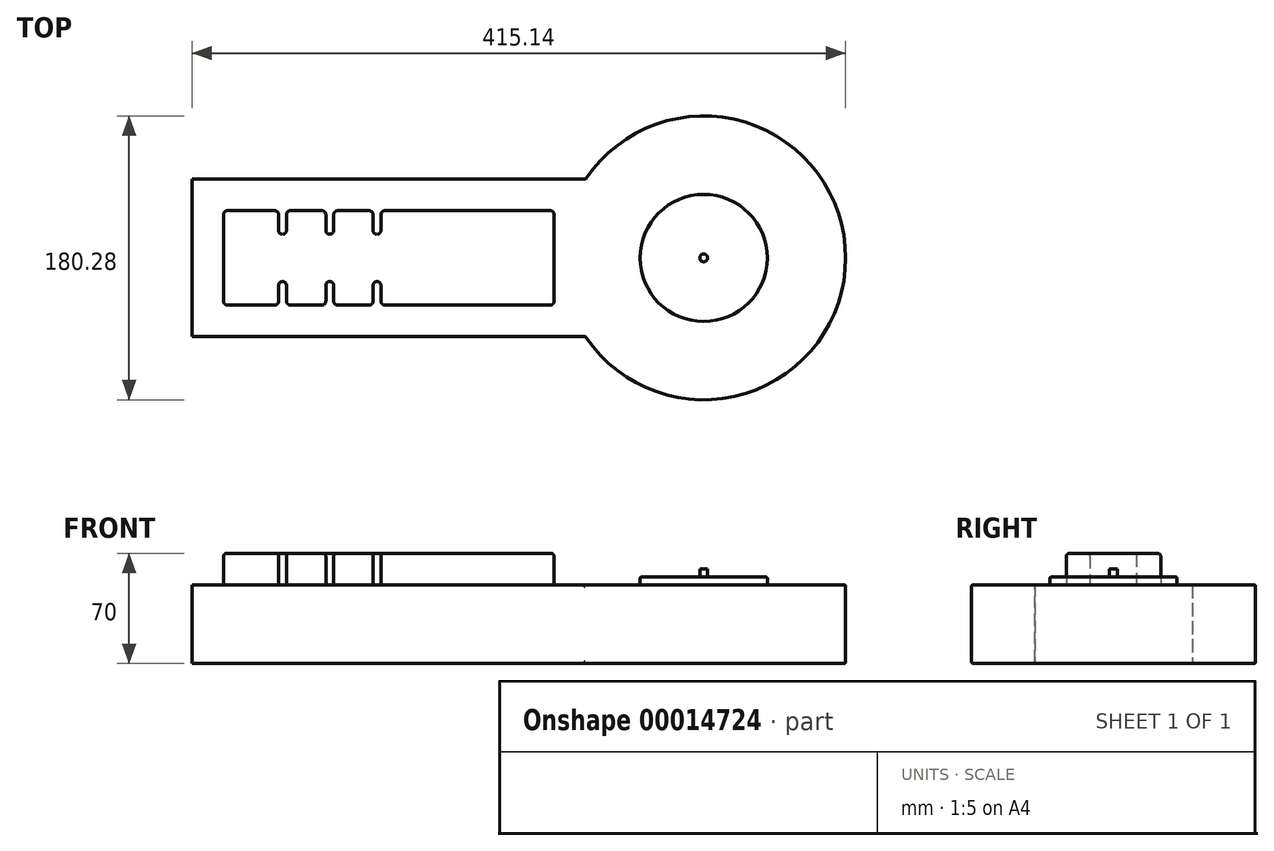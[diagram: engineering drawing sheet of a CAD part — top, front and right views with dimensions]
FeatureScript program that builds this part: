
annotation { "Feature Type Name" : "Feature", "Feature Type Description" : "" }
export const myFeature = defineFeature(function(context is Context, id is Id, definition is map)
    precondition{}
    {
        {
            var Q0;
            Q0=qCreatedBy(makeId("Top.planeOp"),FACE);
            var sketch = newSketch(context, id + "F0", { "sketchPlane" : qUnion([Q0])});
            skLineSegment(sketch, "E0.bottom", {"start": v(0, 0) * mm, "end": v(250, 0) * mm});
            skLineSegment(sketch, "E0.top", {"start": v(0, 100) * mm, "end": v(250, 100) * mm});
            skLineSegment(sketch, "E0.left", {"start": v(0, 0) * mm, "end": v(0, 100) * mm});
            skLineSegment(sketch, "E0.right", {"start": v(250, 0) * mm, "end": v(250, 100) * mm});
            skArc(sketch, "E1", {"start": v(250, 0) * mm, "mid": v(415.14, 50) * mm, "end": v(250, 100) * mm});
            skSolve(sketch);
        }
        {
            var Q0;
            Q0=makeQuery(id+"F0.imprint","IMPRINT",FACE,{"disambiguationData":[TD([[makeQuery(id+"F0.imprint","IMPRINT",EDGE,{"derivedFrom":sQuery(id+"F0.wireOp",EDGE,"E0.bottom")}),1.0]])]});
            var Q1;
            Q1=makeQuery(id+"F0.imprint","IMPRINT",FACE,{"disambiguationData":[TD([[makeQuery(id+"F0.imprint","IMPRINT",EDGE,{"derivedFrom":sQuery(id+"F0.wireOp",EDGE,"E0.right")}),-1.0]])]});
            extrude(context, id + "F1", {"entities" : qUnion([Q0, Q1]), "depth" : 50 * mm});
        }
        {
            var Q0;
            Q0=makeQuery(id+"F1.opExtrude","CAP_FACE",FACE,{"disambiguationData":[OSD([sQuery(id+"F0.wireOp",EDGE,"E0.bottom"),sQuery(id+"F0.wireOp",EDGE,"E0.top"),sQuery(id+"F0.wireOp",EDGE,"E0.left"),sQuery(id+"F0.wireOp",EDGE,"E1")])],"isStart":false});
            var sketch = newSketch(context, id + "F2", { "sketchPlane" : qUnion([Q0])});
            skLineSegment(sketch, "E2.bottom", {"start": v(20, 80) * mm, "end": v(230, 80) * mm});
            skLineSegment(sketch, "E2.top", {"start": v(20, 20) * mm, "end": v(230, 20) * mm});
            skLineSegment(sketch, "E2.left", {"start": v(20, 80) * mm, "end": v(20, 20) * mm});
            skLineSegment(sketch, "E2.right", {"start": v(230, 80) * mm, "end": v(230, 20) * mm});
            skLineSegment(sketch, "E3.bottom", {"start": v(55, 80) * mm, "end": v(60, 80) * mm});
            skLineSegment(sketch, "E3.top", {"start": v(55, 65) * mm, "end": v(60, 65) * mm});
            skLineSegment(sketch, "E3.left", {"start": v(55, 80) * mm, "end": v(55, 65) * mm});
            skLineSegment(sketch, "E3.right", {"start": v(60, 80) * mm, "end": v(60, 65) * mm});
            skLineSegment(sketch, "E4.bottom", {"start": v(85, 80) * mm, "end": v(90, 80) * mm});
            skLineSegment(sketch, "E4.top", {"start": v(85, 65) * mm, "end": v(90, 65) * mm});
            skLineSegment(sketch, "E4.left", {"start": v(85, 80) * mm, "end": v(85, 65) * mm});
            skLineSegment(sketch, "E4.right", {"start": v(90, 80) * mm, "end": v(90, 65) * mm});
            skLineSegment(sketch, "E5.bottom", {"start": v(115, 80) * mm, "end": v(120, 80) * mm});
            skLineSegment(sketch, "E5.top", {"start": v(115, 65) * mm, "end": v(120, 65) * mm});
            skLineSegment(sketch, "E5.left", {"start": v(115, 80) * mm, "end": v(115, 65) * mm});
            skLineSegment(sketch, "E5.right", {"start": v(120, 80) * mm, "end": v(120, 65) * mm});
            skLineSegment(sketch, "E6.bottom", {"start": v(55, 20) * mm, "end": v(60, 20) * mm});
            skLineSegment(sketch, "E6.top", {"start": v(55, 35) * mm, "end": v(60, 35) * mm});
            skLineSegment(sketch, "E6.left", {"start": v(55, 20) * mm, "end": v(55, 35) * mm});
            skLineSegment(sketch, "E6.right", {"start": v(60, 20) * mm, "end": v(60, 35) * mm});
            skLineSegment(sketch, "E7.bottom", {"start": v(85, 20) * mm, "end": v(90, 20) * mm});
            skLineSegment(sketch, "E7.top", {"start": v(85, 35) * mm, "end": v(90, 35) * mm});
            skLineSegment(sketch, "E7.left", {"start": v(85, 20) * mm, "end": v(85, 35) * mm});
            skLineSegment(sketch, "E7.right", {"start": v(90, 20) * mm, "end": v(90, 35) * mm});
            skLineSegment(sketch, "E8.bottom", {"start": v(115, 20) * mm, "end": v(120, 20) * mm});
            skLineSegment(sketch, "E8.top", {"start": v(115, 35) * mm, "end": v(120, 35) * mm});
            skLineSegment(sketch, "E8.left", {"start": v(115, 20) * mm, "end": v(115, 35) * mm});
            skLineSegment(sketch, "E8.right", {"start": v(120, 20) * mm, "end": v(120, 35) * mm});
            skSolve(sketch);
        }
        {
            var Q0;
            {var subQ20=sQuery(id+"F2.wireOp",EDGE,"E2.left");Q0=makeQuery(id+"F2.imprint","IMPRINT",FACE,{"disambiguationData":[TD([[makeQuery(id+"F2.imprint","IMPRINT",EDGE,{"derivedFrom":subQ20}),1.0]])]});}
            extrude(context, id + "F3", {"entities" : qUnion([Q0]), "operationType" : NewBodyOperationType.ADD, "depth" : 20 * mm});
        }
        {
            var Q0;
            Q0=makeQuery(id+"F1.opExtrude","CAP_FACE",FACE,{"disambiguationData":[OSD([sQuery(id+"F0.wireOp",EDGE,"E0.bottom"),sQuery(id+"F0.wireOp",EDGE,"E0.top"),sQuery(id+"F0.wireOp",EDGE,"E0.left"),sQuery(id+"F0.wireOp",EDGE,"E1")])],"isStart":false});
            var sketch = newSketch(context, id + "F4", { "sketchPlane" : qUnion([Q0])});
            skCircle(sketch, "E9", {"center": v(325, 50) * mm, "radius": 40.38 * mm});
            skSolve(sketch);
        }
        {
            var Q0;
            Q0=qSketchRegion(id+"F4",true);
            extrude(context, id + "F5", {"entities" : qUnion([Q0]), "operationType" : NewBodyOperationType.ADD, "depth" : 5 * mm});
        }
        {
            var Q0;
            Q0=makeQuery(id+"F5.opExtrude","CAP_FACE",FACE,{"disambiguationData":[OSD([sQuery(id+"F4.wireOp",EDGE,"E9")])],"isStart":false});
            var sketch = newSketch(context, id + "F6", { "sketchPlane" : qUnion([Q0])});
            skCircle(sketch, "E10", {"center": v(325, 50) * mm, "radius": 2.5 * mm});
            skSolve(sketch);
        }
        {
            var Q0;
            Q0=makeQuery(id+"F6.imprint","IMPRINT",FACE,{"disambiguationData":[TD([[makeQuery(id+"F6.imprint","IMPRINT",EDGE,{"derivedFrom":sQuery(id+"F6.wireOp",EDGE,"E10")}),1.0]])]});
            extrude(context, id + "F7", {"entities" : qUnion([Q0]), "operationType" : NewBodyOperationType.ADD, "depth" : 5 * mm});
        }
        {
            var Q0;
            Q0=makeQuery(id+"F1.opExtrude","SWEPT_FACE",FACE,{"disambiguationData":[OSD([sQuery(id+"F0.wireOp",EDGE,"E1")])]});
            var Q1;
            Q1=makeQuery(id+"F5.opExtrude","CAP_EDGE",EDGE,{"disambiguationData":[OSD([sQuery(id+"F4.wireOp",EDGE,"E9")])],"isStart":false});
            var Q2;
            Q2=makeQuery(id+"F5.opExtrude","CAP_EDGE",EDGE,{"disambiguationData":[OSD([sQuery(id+"F4.wireOp",EDGE,"E9")])],"isStart":true});
            fillet(context, id + "F8", {"entities" : qUnion([Q0, Q1, Q2]), "radius" : 1 * mm, "tangentPropagation" : true, "allowEdgeOverflow" : false});
        }
        {
            var Q0;
            Q0=makeQuery(id+"F3.opExtrude","SWEPT_EDGE",EDGE,{"disambiguationData":[OSD([sQuery(id+"F2.wireOp",EDGE,"E6.top"),sQuery(id+"F2.wireOp",EDGE,"E6.left")])]});
            var Q1;
            Q1=makeQuery(id+"F3.opExtrude","SWEPT_EDGE",EDGE,{"disambiguationData":[OSD([sQuery(id+"F2.wireOp",EDGE,"E2.top"),sQuery(id+"F2.wireOp",EDGE,"E6.bottom"),sQuery(id+"F2.wireOp",EDGE,"E6.left")])]});
            var Q2;
            Q2=makeQuery(id+"F3.opExtrude","SWEPT_EDGE",EDGE,{"disambiguationData":[OSD([sQuery(id+"F2.wireOp",EDGE,"E6.top"),sQuery(id+"F2.wireOp",EDGE,"E6.right")])]});
            var Q3;
            Q3=makeQuery(id+"F3.opExtrude","SWEPT_EDGE",EDGE,{"disambiguationData":[OSD([sQuery(id+"F2.wireOp",EDGE,"E2.top"),sQuery(id+"F2.wireOp",EDGE,"E6.bottom"),sQuery(id+"F2.wireOp",EDGE,"E6.right")])]});
            var Q4;
            Q4=makeQuery(id+"F3.opExtrude","SWEPT_EDGE",EDGE,{"disambiguationData":[OSD([sQuery(id+"F2.wireOp",EDGE,"E2.top"),sQuery(id+"F2.wireOp",EDGE,"E7.bottom"),sQuery(id+"F2.wireOp",EDGE,"E7.left")])]});
            var Q5;
            Q5=makeQuery(id+"F3.opExtrude","SWEPT_EDGE",EDGE,{"disambiguationData":[OSD([sQuery(id+"F2.wireOp",EDGE,"E7.top"),sQuery(id+"F2.wireOp",EDGE,"E7.right")])]});
            var Q6;
            Q6=makeQuery(id+"F3.opExtrude","SWEPT_EDGE",EDGE,{"disambiguationData":[OSD([sQuery(id+"F2.wireOp",EDGE,"E2.top"),sQuery(id+"F2.wireOp",EDGE,"E7.bottom"),sQuery(id+"F2.wireOp",EDGE,"E7.right")])]});
            var Q7;
            Q7=makeQuery(id+"F3.opExtrude","SWEPT_EDGE",EDGE,{"disambiguationData":[OSD([sQuery(id+"F2.wireOp",EDGE,"E2.top"),sQuery(id+"F2.wireOp",EDGE,"E8.bottom"),sQuery(id+"F2.wireOp",EDGE,"E8.left")])]});
            var Q8;
            Q8=makeQuery(id+"F3.opExtrude","SWEPT_EDGE",EDGE,{"disambiguationData":[OSD([sQuery(id+"F2.wireOp",EDGE,"E8.top"),sQuery(id+"F2.wireOp",EDGE,"E8.right")])]});
            var Q9;
            Q9=makeQuery(id+"F3.opExtrude","SWEPT_EDGE",EDGE,{"disambiguationData":[OSD([sQuery(id+"F2.wireOp",EDGE,"E2.top"),sQuery(id+"F2.wireOp",EDGE,"E8.bottom"),sQuery(id+"F2.wireOp",EDGE,"E8.right")])]});
            var Q10;
            Q10=makeQuery(id+"F3.opExtrude","SWEPT_EDGE",EDGE,{"disambiguationData":[OSD([sQuery(id+"F2.wireOp",EDGE,"E7.top"),sQuery(id+"F2.wireOp",EDGE,"E7.left")])]});
            var Q11;
            Q11=makeQuery(id+"F3.opExtrude","SWEPT_EDGE",EDGE,{"disambiguationData":[OSD([sQuery(id+"F2.wireOp",EDGE,"E8.top"),sQuery(id+"F2.wireOp",EDGE,"E8.left")])]});
            var Q12;
            Q12=makeQuery(id+"F3.opExtrude","SWEPT_EDGE",EDGE,{"disambiguationData":[OSD([sQuery(id+"F2.wireOp",EDGE,"E3.top"),sQuery(id+"F2.wireOp",EDGE,"E3.left")])]});
            var Q13;
            Q13=makeQuery(id+"F3.opExtrude","SWEPT_EDGE",EDGE,{"disambiguationData":[OSD([sQuery(id+"F2.wireOp",EDGE,"E2.bottom"),sQuery(id+"F2.wireOp",EDGE,"E3.bottom"),sQuery(id+"F2.wireOp",EDGE,"E3.left")])]});
            var Q14;
            Q14=makeQuery(id+"F3.opExtrude","SWEPT_EDGE",EDGE,{"disambiguationData":[OSD([sQuery(id+"F2.wireOp",EDGE,"E4.top"),sQuery(id+"F2.wireOp",EDGE,"E4.left")])]});
            var Q15;
            Q15=makeQuery(id+"F3.opExtrude","SWEPT_EDGE",EDGE,{"disambiguationData":[OSD([sQuery(id+"F2.wireOp",EDGE,"E2.bottom"),sQuery(id+"F2.wireOp",EDGE,"E4.bottom"),sQuery(id+"F2.wireOp",EDGE,"E4.left")])]});
            var Q16;
            Q16=makeQuery(id+"F3.opExtrude","SWEPT_EDGE",EDGE,{"disambiguationData":[OSD([sQuery(id+"F2.wireOp",EDGE,"E5.top"),sQuery(id+"F2.wireOp",EDGE,"E5.left")])]});
            var Q17;
            Q17=makeQuery(id+"F3.opExtrude","SWEPT_EDGE",EDGE,{"disambiguationData":[OSD([sQuery(id+"F2.wireOp",EDGE,"E2.bottom"),sQuery(id+"F2.wireOp",EDGE,"E5.bottom"),sQuery(id+"F2.wireOp",EDGE,"E5.left")])]});
            var Q18;
            Q18=makeQuery(id+"F3.opExtrude","SWEPT_EDGE",EDGE,{"disambiguationData":[OSD([sQuery(id+"F2.wireOp",EDGE,"E3.top"),sQuery(id+"F2.wireOp",EDGE,"E3.right")])]});
            var Q19;
            Q19=makeQuery(id+"F3.opExtrude","SWEPT_EDGE",EDGE,{"disambiguationData":[OSD([sQuery(id+"F2.wireOp",EDGE,"E2.bottom"),sQuery(id+"F2.wireOp",EDGE,"E3.bottom"),sQuery(id+"F2.wireOp",EDGE,"E3.right")])]});
            var Q20;
            Q20=makeQuery(id+"F3.opExtrude","SWEPT_EDGE",EDGE,{"disambiguationData":[OSD([sQuery(id+"F2.wireOp",EDGE,"E4.top"),sQuery(id+"F2.wireOp",EDGE,"E4.right")])]});
            var Q21;
            Q21=makeQuery(id+"F3.opExtrude","SWEPT_EDGE",EDGE,{"disambiguationData":[OSD([sQuery(id+"F2.wireOp",EDGE,"E2.bottom"),sQuery(id+"F2.wireOp",EDGE,"E4.bottom"),sQuery(id+"F2.wireOp",EDGE,"E4.right")])]});
            var Q22;
            Q22=makeQuery(id+"F3.opExtrude","SWEPT_EDGE",EDGE,{"disambiguationData":[OSD([sQuery(id+"F2.wireOp",EDGE,"E5.top"),sQuery(id+"F2.wireOp",EDGE,"E5.right")])]});
            var Q23;
            Q23=makeQuery(id+"F3.opExtrude","SWEPT_EDGE",EDGE,{"disambiguationData":[OSD([sQuery(id+"F2.wireOp",EDGE,"E2.bottom"),sQuery(id+"F2.wireOp",EDGE,"E5.bottom"),sQuery(id+"F2.wireOp",EDGE,"E5.right")])]});
            var Q24;
            Q24=makeQuery(id+"F3.opExtrude","SWEPT_EDGE",EDGE,{"disambiguationData":[OSD([sQuery(id+"F2.wireOp",EDGE,"E2.bottom"),sQuery(id+"F2.wireOp",EDGE,"E2.left")])]});
            var Q25;
            Q25=makeQuery(id+"F3.opExtrude","SWEPT_EDGE",EDGE,{"disambiguationData":[OSD([sQuery(id+"F2.wireOp",EDGE,"E2.top"),sQuery(id+"F2.wireOp",EDGE,"E2.left")])]});
            var Q26;
            Q26=makeQuery(id+"F3.opExtrude","SWEPT_EDGE",EDGE,{"disambiguationData":[OSD([sQuery(id+"F2.wireOp",EDGE,"E2.bottom"),sQuery(id+"F2.wireOp",EDGE,"E2.right")])]});
            var Q27;
            Q27=makeQuery(id+"F3.opExtrude","SWEPT_EDGE",EDGE,{"disambiguationData":[OSD([sQuery(id+"F2.wireOp",EDGE,"E2.top"),sQuery(id+"F2.wireOp",EDGE,"E2.right")])]});
            fillet(context, id + "F9", {"entities" : qUnion([Q0, Q1, Q2, Q3, Q4, Q5, Q6, Q7, Q8, Q9, Q10, Q11, Q12, Q13, Q14, Q15, Q16, Q17, Q18, Q19, Q20, Q21, Q22, Q23, Q24, Q25, Q26, Q27]), "radius" : 2.5 * mm, "tangentPropagation" : true, "allowEdgeOverflow" : false});
        }
        {
            var Q0;
            {var subQ0=sQuery(id+"F2.wireOp",EDGE,"E2.bottom");Q0=makeQuery(id+"F3.opExtrude","CAP_EDGE",EDGE,{"disambiguationData":[OSD([subQ0]),TDD([makeQuery(id+"F2.imprint","IMPRINT",EDGE,{"disambiguationData":[TD([[makeQuery(id+"F2.imprint","INTERSECT",VERTEX,{"derivedFrom":[subQ0,sQuery(id+"F2.wireOp",EDGE,"E2.right")]}),1.0]])],"derivedFrom":subQ0})])],"isStart":false});}
            var Q1;
            Q1=makeQuery(id+"F3.opExtrude","CAP_EDGE",EDGE,{"disambiguationData":[OSD([sQuery(id+"F2.wireOp",EDGE,"E2.right")])],"isStart":false});
            fillet(context, id + "F10", {"entities" : qUnion([Q0, Q1]), "radius" : 2 * mm, "tangentPropagation" : true, "allowEdgeOverflow" : false});
        }
    });
